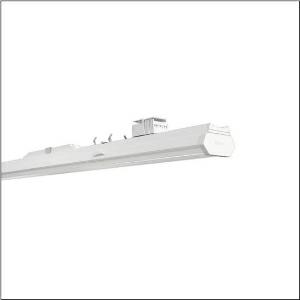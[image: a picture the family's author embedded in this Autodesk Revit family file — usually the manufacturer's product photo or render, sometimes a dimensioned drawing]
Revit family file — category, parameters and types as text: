
# Revit family: licross_r__11_protected_ho_51ts12dn4dxld_51d4
name_source: partatom
category: Lighting Fixtures
units: mm (PartAtom-declared; Revit-internal decimal feet)

## family parameters
Cut with Voids When Loaded = No
Host = Face
Light Source = No
Part Type = Normal
Room Calculation Point = No
Round Connector Dimension = Use Diameter
Shared = No

## types (1)
- --- (1 x LED, 2100 lm, 14.7 W, 4000K)
    Apparent Load = 15 VA
    CIE Flux Codes = 54 82 95 97 100
    Color Rendering = 80
    Color Temperature = 4000K
    Default Elevation = 1800 mm
    Description = Licross® 11 Protected HOluminaire insert, length: 1.500mm, width: 90mm, height: 101mm, LED rated luminous flux: 13.360lm, light colour: 840, control gear: DALI 2, control gear: ECG DALI, with plug, 6-pole, with phase selection, mains connection: 220..240V, AC/DC, 0/50..60Hz, without changeover relay, for emergency light function, for central battery installations according to DIN EN 60598-2-22, halogen-free wiring, primary optical cover: cover, of PMMA, light emission: direct with ceiling illumination distribution, protection rating (complete): IP50, insulation class (complete): insulation class I (protective earthing), certification: CE, ENEC, VDE, protection symbol: D if used in an environment without relevant dust loads with corresponding accessories, permissible ambient temperature for indoor applications: -25..+35°C, standard: EN 60598-2-22, reducing of maximum allowable ambient temperature of 5°C with ceiling mounting, corresponds to IFS (International Featured Standards) requirements for safety and quality in the food industry, packaging unit: 1 piece
    Height = 92 mm
    Lamp = 1 x LED
    Lamp Light Flux = 2100 lm
    Lamp Power = 14.7 W
    Lamp count = 1
    Length = 1500 mm
    Luminous efficacy = 143 lm/W
    Manufacturer = Siteco
    ModVariant = No
    Model = 51TS12DN4DXLD
    Mounting Place = Ceiling
    Mounting Type = Pendant
    Number of Poles = 1
    OnlyDefault = Yes
    Power Factor = 1
    Product Name = Licross® 11 Protected HO
    Product group = luminaire insert
    ProductGroupID = 902
    Protection Class = Protection class I
    Protection Degree = IP 50
    RLX_Detail_Level = 1
    RlxData = <blob elided: 24417 chars, md5=28d737c9>
    Socket = socket
    Standby Power = 0 W
    System Light Flux = 2100 lm
    System Power = 15 W
    Type Comments = : DC mode (central or group accumulator) initial emergency light level
    Type Image = l_1256145.jpg
    URL = http://relux.com
    VarID = @adj_134905
    Voltage = 0 V
    Weight = 0.00 kg
    Width = 88 mm

## geometry (parser evidence)
native form markers: Blend x4, Sweep x11
no freeform markers — native parametric forms only
